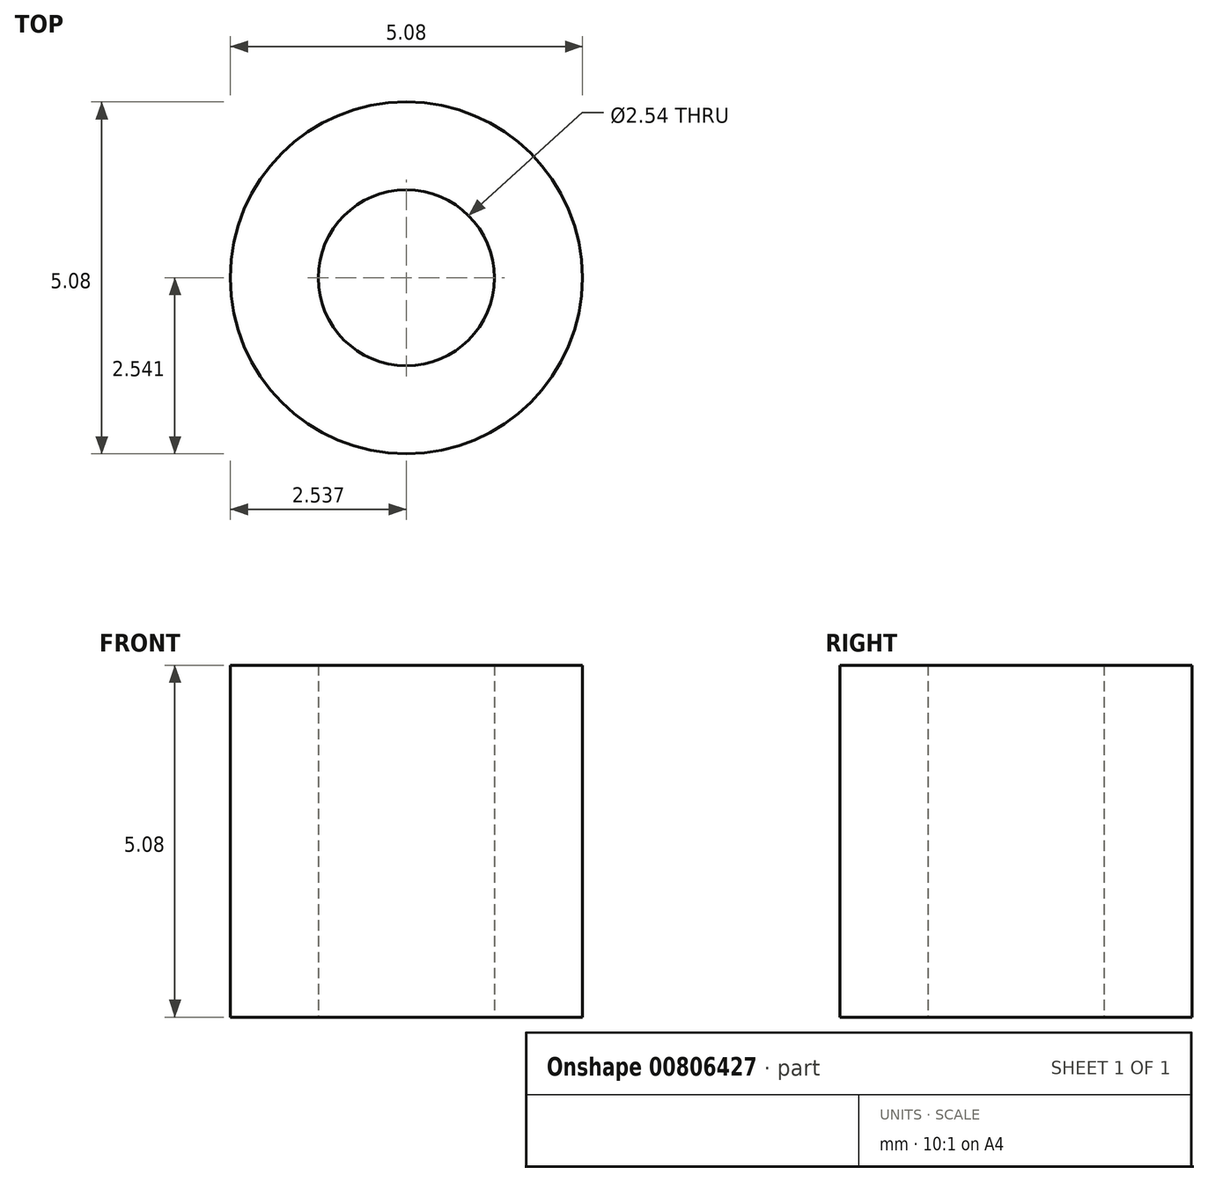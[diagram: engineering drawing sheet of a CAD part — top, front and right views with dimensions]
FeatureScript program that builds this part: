
annotation { "Feature Type Name" : "Feature", "Feature Type Description" : "" }
export const myFeature = defineFeature(function(context is Context, id is Id, definition is map)
    precondition{}
    {
        {
            var Q0;
            Q0=qCreatedBy(makeId("Top.planeOp"),FACE);
            var sketch = newSketch(context, id + "F0", { "sketchPlane" : qUnion([Q0])});
            skCircle(sketch, "E0", {"center": v(-42.45, 33.85) * mm, "radius": 12.2 * mm});
            skPoint(sketch, "E0.first.point", {"position": v(-48.85, 44.23) * mm});
            skPoint(sketch, "E0.second.point", {"position": v(-31.35, 28.83) * mm});
            skPoint(sketch, "E0.third.point", {"position": v(-51, 25.16) * mm});
            skSolve(sketch);
        }
        {
            var Q0;
            Q0 = qSketchRegion(id + "F0", true);
            extrude(context, id + "F1", {"entities" : qUnion([Q0]), "depth" : 24.13 * mm, "offsetDistance" : 25.4 * mm});
        }
        {
            var Q0;
            Q0=makeQuery(id+"F1.opExtrude","SWEPT_BODY",BODY,{"disambiguationData":[OSD([sQuery(id+"F0.wireOp",EDGE,"E0")])]});
            deleteBodies(context, id + "F2", {"entities" : qUnion([Q0])});
        }
        {
            var Q0;
            Q0=qCreatedBy(makeId("Top.planeOp"),FACE);
            var sketch = newSketch(context, id + "F3", { "sketchPlane" : qUnion([Q0])});
            skCircle(sketch, "E1", {"center": v(-29.81, 4.15) * mm, "radius": 2.54 * mm});
            skPoint(sketch, "E1.first.point", {"position": v(-30.65, 6.55) * mm});
            skPoint(sketch, "E1.second.point", {"position": v(-27.3, 3.74) * mm});
            skPoint(sketch, "E1.third.point", {"position": v(-30.44, 1.69) * mm});
            skSolve(sketch);
        }
        {
            var Q0;
            Q0 = qSketchRegion(id + "F3", true);
            extrude(context, id + "F4", {"entities" : qUnion([Q0]), "depth" : 5.08 * mm, "offsetDistance" : 25.4 * mm});
        }
        {
            var Q0;
            Q0=qCreatedBy(makeId("Top.planeOp"),FACE);
            var sketch = newSketch(context, id + "F5", { "sketchPlane" : qUnion([Q0])});
            skCircle(sketch, "E2", {"center": v(-29.81, 4.15) * mm, "radius": 1.27 * mm});
            skPoint(sketch, "E2.first.point", {"position": v(-30.7, 5.07) * mm});
            skPoint(sketch, "E2.second.point", {"position": v(-29.19, 3.05) * mm});
            skPoint(sketch, "E2.third.point", {"position": v(-29.97, 2.9) * mm});
            skSolve(sketch);
        }
        {
            var Q0;
            Q0 = qSketchRegion(id + "F5", true);
            extrude(context, id + "F6", {"entities" : qUnion([Q0]), "operationType" : NewBodyOperationType.REMOVE, "endBound" : BoundingType.SYMMETRIC, "depth" : 25.4 * mm, "offsetDistance" : 25.4 * mm});
        }
    });
